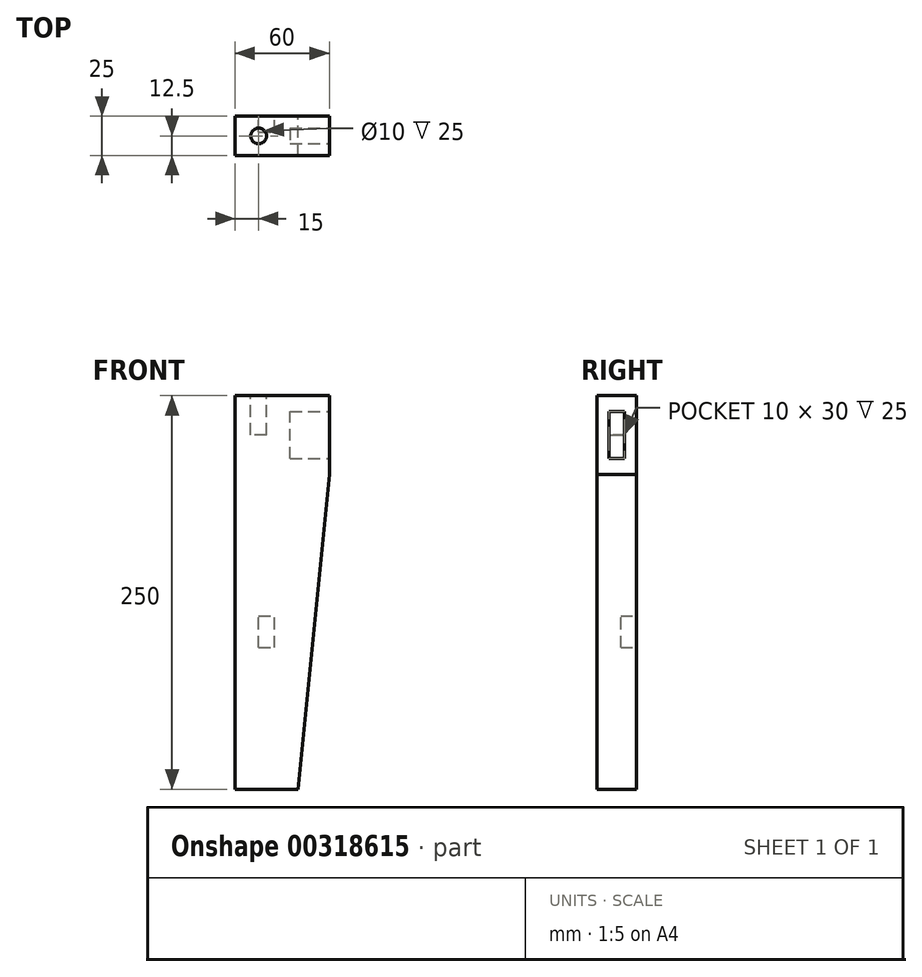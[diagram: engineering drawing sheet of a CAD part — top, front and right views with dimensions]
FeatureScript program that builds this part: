
annotation { "Feature Type Name" : "Feature", "Feature Type Description" : "" }
export const myFeature = defineFeature(function(context is Context, id is Id, definition is map)
    precondition{}
    {
        {
            var Q0;
            Q0=qCreatedBy(makeId("Front.planeOp"),FACE);
            var sketch = newSketch(context, id + "F0", { "sketchPlane" : qUnion([Q0])});
            skLineSegment(sketch, "E0", {"start": v(0, 0) * mm, "end": v(20, 200) * mm});
            skLineSegment(sketch, "E1", {"start": v(20, 200) * mm, "end": v(20, 250) * mm});
            skLineSegment(sketch, "E2", {"start": v(20, 250) * mm, "end": v(-40, 250) * mm});
            skLineSegment(sketch, "E3", {"start": v(-40, 250) * mm, "end": v(-40, 0) * mm});
            skLineSegment(sketch, "E4", {"start": v(-40, 0) * mm, "end": v(0, 0) * mm});
            skSolve(sketch);
        }
        {
            var Q0;
            Q0=qSketchRegion(id+"F0",true);
            extrude(context, id + "F1", {"entities" : qUnion([Q0]), "endBound" : BoundingType.SYMMETRIC, "depth" : 25 * mm});
        }
        {
            var Q0;
            Q0=makeQuery(id+"F1.opExtrude","SWEPT_FACE",FACE,{"disambiguationData":[OSD([sQuery(id+"F0.wireOp",EDGE,"E1")])]});
            var sketch = newSketch(context, id + "F2", { "sketchPlane" : qUnion([Q0])});
            skLineSegment(sketch, "E5", {"start": v(0, 200) * mm, "end": v(0, 250) * mm, "construction": true});
            skLineSegment(sketch, "E6.rect.bottom", {"start": v(5, 210) * mm, "end": v(-5, 210) * mm});
            skLineSegment(sketch, "E6.rect.top", {"start": v(5, 240) * mm, "end": v(-5, 240) * mm});
            skLineSegment(sketch, "E6.rect.left", {"start": v(5, 210) * mm, "end": v(5, 240) * mm});
            skLineSegment(sketch, "E6.rect.right", {"start": v(-5, 210) * mm, "end": v(-5, 240) * mm});
            skPoint(sketch, "E6.rect.middle", {"position": v(0, 225) * mm});
            skSolve(sketch);
        }
        {
            var Q0;
            Q0=qSketchRegion(id+"F2",true);
            extrude(context, id + "F3", {"entities" : qUnion([Q0]), "operationType" : NewBodyOperationType.REMOVE, "oppositeDirection" : true, "depth" : 25 * mm});
        }
        {
            var Q0;
            Q0=makeQuery(id+"F1.opExtrude","CAP_FACE",FACE,{"disambiguationData":[OSD([sQuery(id+"F0.wireOp",EDGE,"E0"),sQuery(id+"F0.wireOp",EDGE,"E1"),sQuery(id+"F0.wireOp",EDGE,"E2"),sQuery(id+"F0.wireOp",EDGE,"E3"),sQuery(id+"F0.wireOp",EDGE,"E4")])],"isStart":true});
            var sketch = newSketch(context, id + "F4", { "sketchPlane" : qUnion([Q0])});
            skLineSegment(sketch, "E7.rect.bottom", {"start": v(25, 90) * mm, "end": v(15, 90) * mm});
            skLineSegment(sketch, "E7.rect.top", {"start": v(25, 110) * mm, "end": v(15, 110) * mm});
            skLineSegment(sketch, "E7.rect.left", {"start": v(25, 90) * mm, "end": v(25, 110) * mm});
            skLineSegment(sketch, "E7.rect.right", {"start": v(15, 90) * mm, "end": v(15, 110) * mm});
            skPoint(sketch, "E7.rect.middle", {"position": v(20, 100) * mm});
            skSolve(sketch);
        }
        {
            var Q0;
            Q0=qSketchRegion(id+"F4",true);
            extrude(context, id + "F5", {"entities" : qUnion([Q0]), "operationType" : NewBodyOperationType.REMOVE, "oppositeDirection" : true, "depth" : 10 * mm});
        }
        {
            var Q0;
            Q0=makeQuery(id+"F1.opExtrude","SWEPT_FACE",FACE,{"disambiguationData":[OSD([sQuery(id+"F0.wireOp",EDGE,"E2")])]});
            var sketch = newSketch(context, id + "F6", { "sketchPlane" : qUnion([Q0])});
            skLineSegment(sketch, "E8", {"start": v(20, 0) * mm, "end": v(-40, 0) * mm, "construction": true});
            skCircle(sketch, "E9", {"center": v(-25, 0) * mm, "radius": 5 * mm});
            skSolve(sketch);
        }
        {
            var Q0;
            Q0=qSketchRegion(id+"F6",true);
            extrude(context, id + "F7", {"entities" : qUnion([Q0]), "operationType" : NewBodyOperationType.REMOVE, "oppositeDirection" : true, "depth" : 25 * mm});
        }
    });
